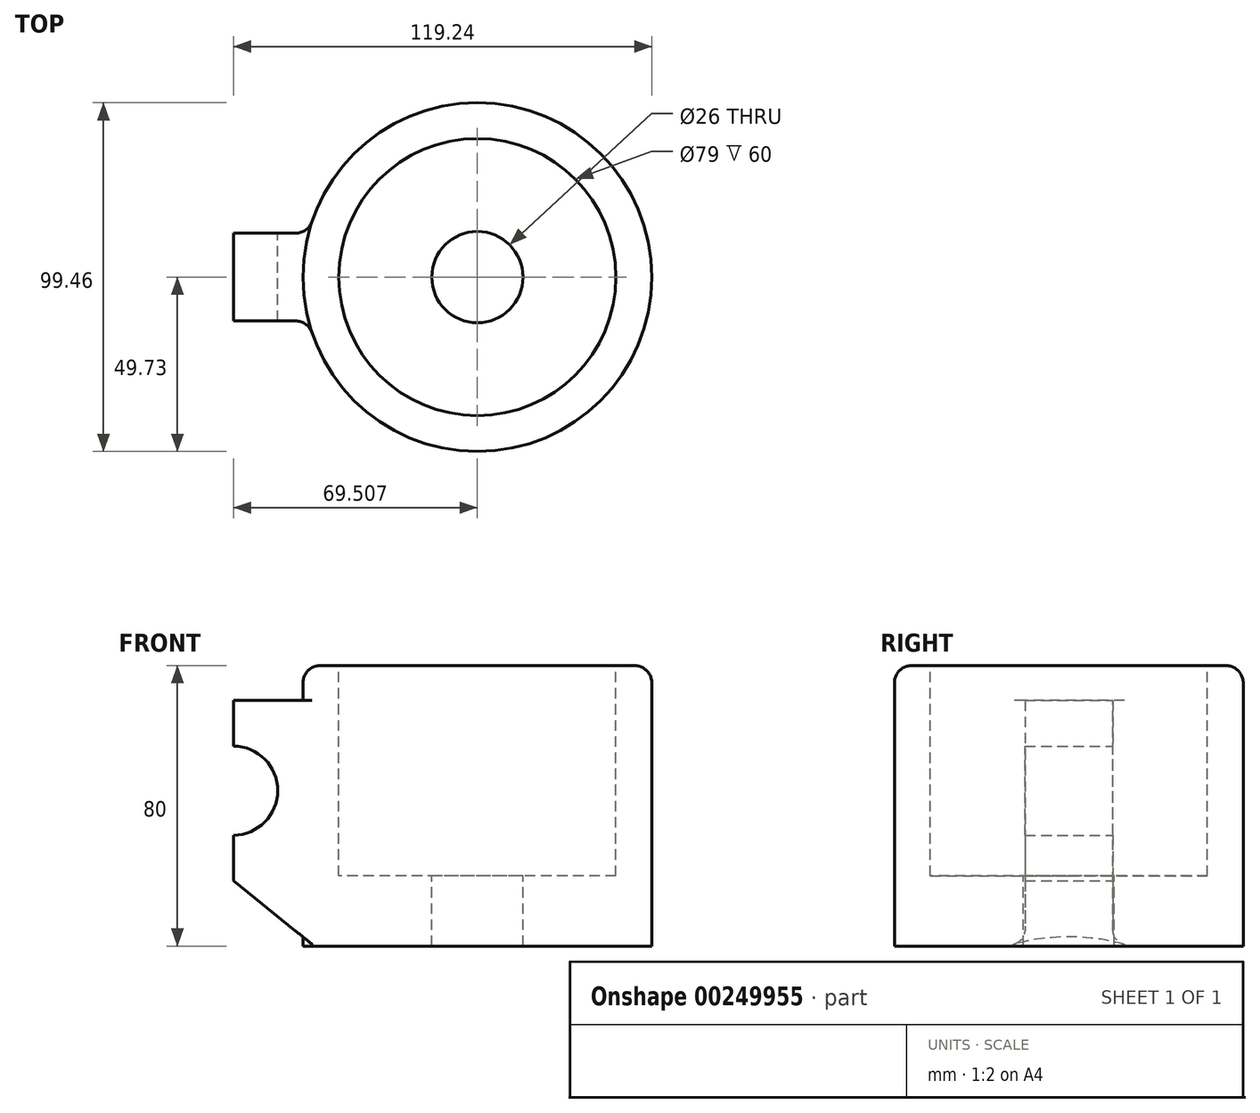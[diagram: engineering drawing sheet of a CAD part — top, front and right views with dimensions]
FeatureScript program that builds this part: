
annotation { "Feature Type Name" : "Feature", "Feature Type Description" : "" }
export const myFeature = defineFeature(function(context is Context, id is Id, definition is map)
    precondition{}
    {
        {
            var Q0;
            Q0=qCreatedBy(makeId("Front.planeOp"),FACE);
            var sketch = newSketch(context, id + "F0", { "sketchPlane" : qUnion([Q0])});
            skLineSegment(sketch, "E0", {"start": v(0, 0) * mm, "end": v(-23, 0) * mm});
            skLineSegment(sketch, "E1", {"start": v(-23, 0) * mm, "end": v(-23, -13) * mm});
            skArc(sketch, "E2", {"start": v(-23, -38.4) * mm, "mid": v(-10.42, -25.7) * mm, "end": v(-23, -13) * mm});
            skLineSegment(sketch, "E3", {"start": v(-23, -38.4) * mm, "end": v(-23, -51.4) * mm});
            skLineSegment(sketch, "E4", {"start": v(-23, -51.4) * mm, "end": v(0, -70) * mm});
            skLineSegment(sketch, "E5", {"start": v(0, -70) * mm, "end": v(0, 0) * mm});
            skSolve(sketch);
        }
        {
            var Q0;
            Q0=makeQuery(id+"F0.imprint","IMPRINT",FACE,{"disambiguationData":[TD([[makeQuery(id+"F0.imprint","IMPRINT",EDGE,{"derivedFrom":sQuery(id+"F0.wireOp",EDGE,"E0")}),1.0]])]});
            extrude(context, id + "F1", {"entities" : qUnion([Q0]), "endBound" : BoundingType.SYMMETRIC, "depth" : 25 * mm});
        }
        {
            var Q0;
            Q0=qCreatedBy(makeId("Top.planeOp"),FACE);
            var sketch = newSketch(context, id + "F2", { "sketchPlane" : qUnion([Q0])});
            skCircle(sketch, "E6", {"center": v(46.5, 0) * mm, "radius": 49.73 * mm});
            skSolve(sketch);
        }
        {
            var Q0;
            Q0=makeQuery(id+"F2.imprint","IMPRINT",FACE,{"disambiguationData":[TD([[makeQuery(id+"F2.imprint","IMPRINT",EDGE,{"derivedFrom":sQuery(id+"F2.wireOp",EDGE,"E6")}),1.0]])]});
            var Q1;
            Q1 = qSketchRegion(id + "F4", true);
            extrude(context, id + "F3", {"entities" : qUnion([Q0, Q1]), "operationType" : NewBodyOperationType.ADD, "oppositeDirection" : true, "depth" : 70 * mm});
        }
        {
            var Q0;
            Q0=makeQuery(id+"F3.boolean.opBoolean","MERGE",FACE,{"derivedFrom":[makeQuery(id+"F1.opExtrude","SWEPT_FACE",FACE,{"disambiguationData":[OSD([sQuery(id+"F0.wireOp",EDGE,"E0")])]}),makeQuery(id+"F3.opExtrude","CAP_FACE",FACE,{"disambiguationData":[OSD([sQuery(id+"F2.wireOp",EDGE,"E6")])],"isStart":true})]});
            var sketch = newSketch(context, id + "F4", { "sketchPlane" : qUnion([Q0])});
            skSolve(sketch);
        }
        {
            var Q0;
            Q0 = qSketchRegion(id + "F2", true);
            extrude(context, id + "F5", {"entities" : qUnion([Q0]), "operationType" : NewBodyOperationType.ADD, "depth" : 10 * mm});
        }
        {
            var Q0;
            Q0=makeQuery(id+"F5.opExtrude","CAP_FACE",FACE,{"disambiguationData":[OSD([sQuery(id+"F2.wireOp",EDGE,"E6")])],"isStart":false});
            cPlane(context, id + "F6", {"entities" : qUnion([Q0]), "cplaneType" : CPlaneType.OFFSET, "offset" : 0 * mm, "width" : 150 * mm, "height" : 150 * mm});
        }
        {
            var Q0;
            Q0=makeQuery(id+"F5.opExtrude","CAP_FACE",FACE,{"disambiguationData":[OSD([sQuery(id+"F2.wireOp",EDGE,"E6")])],"isStart":false});
            var sketch = newSketch(context, id + "F7", { "sketchPlane" : qUnion([Q0])});
            skCircle(sketch, "E7", {"center": v(46.5, 0) * mm, "radius": 39.5 * mm});
            skSolve(sketch);
        }
        {
            var Q0;
            Q0=sQuery(id+"F7.wireOp",VERTEX,"E7.center");
            var Q1;
            Q1=makeQuery(id+"F1.opExtrude","SWEPT_BODY",BODY,{"disambiguationData":[OSD([sQuery(id+"F0.wireOp",EDGE,"E0"),sQuery(id+"F0.wireOp",EDGE,"E1"),sQuery(id+"F0.wireOp",EDGE,"E2"),sQuery(id+"F0.wireOp",EDGE,"E3"),sQuery(id+"F0.wireOp",EDGE,"E4"),sQuery(id+"F0.wireOp",EDGE,"E5")])]});
            hole(context, id + "F8", {"style" : HoleStyle.C_BORE, "endStyle" : HoleEndStyle.THROUGH, "holeDiameter" : 26 * mm, "cBoreDiameter" : 79 * mm, "cBoreDepth" : 60 * mm, "tappedDepth" : 12 * mm, "tapClearance" : 3, "locations" : qUnion([Q0]), "scope" : qUnion([Q1])});
        }
        {
            var Q0;
            Q0=makeQuery(id+"F5.opExtrude","CAP_EDGE",EDGE,{"disambiguationData":[OSD([sQuery(id+"F2.wireOp",EDGE,"E6")])],"isStart":false});
            fillet(context, id + "F9", {"entities" : qUnion([Q0]), "radius" : 5 * mm, "tangentPropagation" : true, "allowEdgeOverflow" : false});
        }
        {
            var Q0;
            Q0=makeQuery(id+"F3.boolean.opBoolean","INTERSECT",EDGE,{"derivedFrom":[makeQuery(id+"F1.opExtrude","CAP_FACE",FACE,{"disambiguationData":[OSD([sQuery(id+"F0.wireOp",EDGE,"E0"),sQuery(id+"F0.wireOp",EDGE,"E1"),sQuery(id+"F0.wireOp",EDGE,"E2"),sQuery(id+"F0.wireOp",EDGE,"E3"),sQuery(id+"F0.wireOp",EDGE,"E4"),sQuery(id+"F0.wireOp",EDGE,"E5")])],"isStart":true}),makeQuery(id+"F3.opExtrude","SWEPT_FACE",FACE,{"disambiguationData":[OSD([sQuery(id+"F2.wireOp",EDGE,"E6")])]})]});
            var Q1;
            Q1=makeQuery(id+"F3.boolean.opBoolean","INTERSECT",EDGE,{"derivedFrom":[makeQuery(id+"F1.opExtrude","CAP_FACE",FACE,{"disambiguationData":[OSD([sQuery(id+"F0.wireOp",EDGE,"E0"),sQuery(id+"F0.wireOp",EDGE,"E1"),sQuery(id+"F0.wireOp",EDGE,"E2"),sQuery(id+"F0.wireOp",EDGE,"E3"),sQuery(id+"F0.wireOp",EDGE,"E4"),sQuery(id+"F0.wireOp",EDGE,"E5")])],"isStart":false}),makeQuery(id+"F3.opExtrude","SWEPT_FACE",FACE,{"disambiguationData":[OSD([sQuery(id+"F2.wireOp",EDGE,"E6")])]})]});
            var Q2;
            Q2=makeQuery(id+"F5.opExtrude","CAP_EDGE",EDGE,{"disambiguationData":[OSD([sQuery(id+"F2.wireOp",EDGE,"E6")])],"isStart":true});
            fillet(context, id + "F10", {"entities" : qUnion([Q0, Q1, Q2]), "radius" : 5 * mm, "tangentPropagation" : true, "allowEdgeOverflow" : false});
        }
    });
